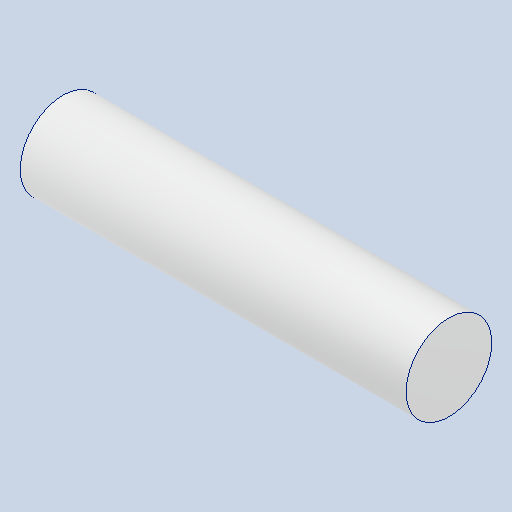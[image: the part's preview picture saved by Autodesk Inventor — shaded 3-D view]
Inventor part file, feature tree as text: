
AUTODESK INVENTOR PART (.ipt)
format: ipt  version: 2024.3 (Build 283343000, 343)  size: 227,840 bytes
history: native  units: mm
features: other x1, extrude x1, sketch x1
ambient origin geometry x8: Origin, YZ Plane, XZ Plane, XY Plane, X Axis, Y Axis, Z Axis, Center Point
bodies: Body1 (feature_tree)
feature tree (3):
  other  "ソリッド1"
  extrude  "押し出し1"  Depth=10.0mm
  sketch  "スケッチ1"
